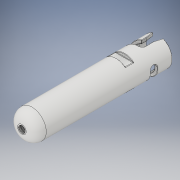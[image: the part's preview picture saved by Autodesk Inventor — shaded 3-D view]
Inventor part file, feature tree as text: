
AUTODESK INVENTOR PART (.ipt)
format: ipt  version: 2019 (Build 230136000, 136)  size: 1,806,848 bytes
history: native  units: mm
features: other x7, fillet x4, sketch x4, extrude x3, chamfer x3, pattern_circular x1, mirror x1
ambient origin geometry x8: Origin, YZ Plane, XZ Plane, XY Plane, X Axis, Y Axis, Z Axis, Center Point
bodies: Solide1 (feature_tree)
feature tree (23):
  other  "Révolution1"
  other  "Plan de construction1"
  extrude  "Extrusion2"  Depth=6.0mm
  other  "Hélicoïde1"
  extrude  "Extrusion3"  Depth=27.576202mm
  fillet  "Congé2"  Radius=2.2mm
  fillet  "Congé3"  Radius=2.2mm
  fillet  "Congé4"  Radius=0.5mm
  chamfer  "Chanfrein2"  Angle=90.0deg  [1 undecoded]
  chamfer  "Chanfrein3"  Distance=20.0mm
  fillet  "Congé5"  Radius=0.5mm
  pattern_circular  "Réseau circulaire1"  [2 undecoded]
  extrude  "Extrusion4"  Depth=100.0mm
  chamfer  "Chanfrein4"  Distance=0.2mm
  mirror  "Symétrie1"
  sketch  "Esquisse1"
  sketch  "Esquisse4"
  sketch  "Esquisse5"
  sketch  "Esquisse6"
  other  "Projeter les arêtes coupées2"
  other  "Projeter les arêtes coupées3"
  other  "Projeter les arêtes coupées4"
  other  "Projeter les arêtes coupées5"
note: 3 required parameter values undecoded (feature->parameter linkage not recoverable at this tier; creation-order binding heuristic only, values carry confidence <= 0.55)
